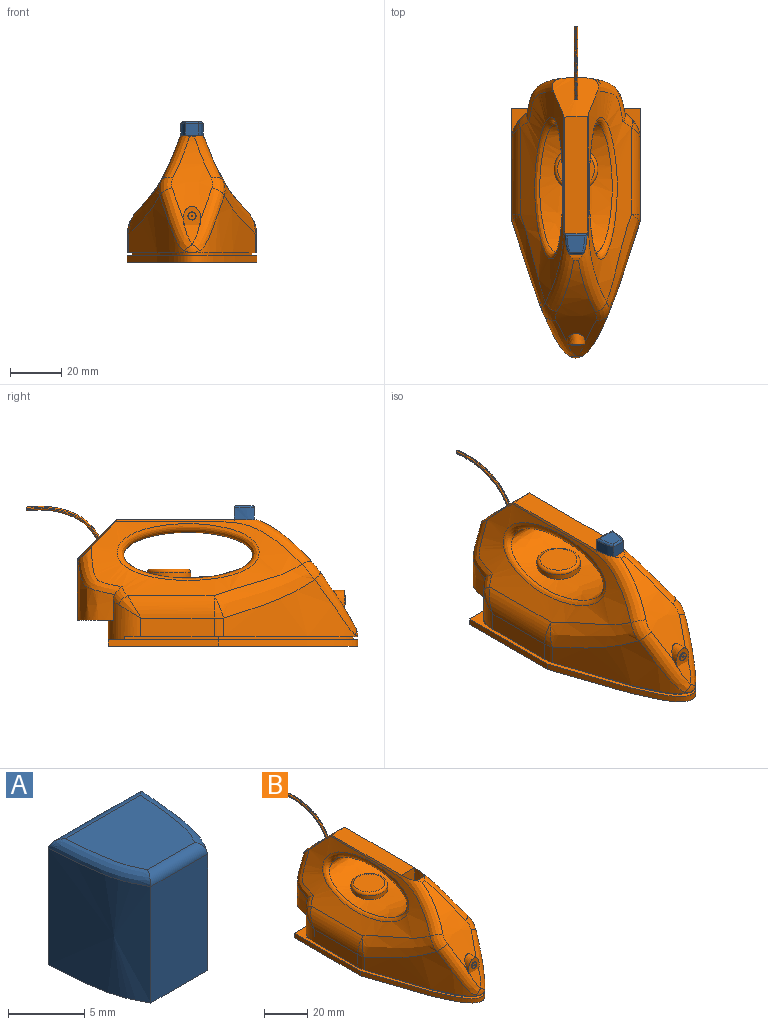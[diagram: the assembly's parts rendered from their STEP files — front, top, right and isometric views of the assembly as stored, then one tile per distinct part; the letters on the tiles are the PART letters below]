
ASSEMBLY  parts=2 mates=1
PART A: 10 faces, bbox 8.7x9.4x10.1 mm
  f0: extruded ~9.37x7.84mm, area 76.1mm2, adj f1,f3,f5,f6
  f1: plane 9.37x8.64mm, normal (0,1,0), area 81mm2, adj f0,f2,f5,f7
  f2: extruded ~9.37x7.84mm, area 76mm2, adj f1,f3,f5,f9
  f3: plane 9.37x5.27mm, normal (0,-1,0), area 49.4mm2, adj f0,f2,f5,f8
  f4: plane 7.01x6.32mm, normal (0,0,1), area 39mm2, adj f6,f7,f8,f9
  f5: plane 8.64x7.84mm, normal (0,0,-1), area 59.8mm2, adj f0,f1,f2,f3
  f6: bspline ~9.22x2.92mm, area 8.8mm2, adj f0,f4,f7,f8
  f7: cylinder r=0.76mm len=8.64mm, axis (1,0,0), area 9.4mm2, adj f1,f4,f6,f9
  f8: cylinder r=0.76mm len=5.27mm, axis (-1,0,0), area 5.8mm2, adj f3,f4,f6,f9
  f9: bspline ~8.95x2.65mm, area 8.8mm2, adj f2,f4,f7,f8
PART B: 393 faces, bbox 51x148.2x55 mm
  f0: extruded ~50.42x28.36mm, area 1593mm2, adj f1,f4,f385
  f1: cylinder r=8.53mm len=17.06mm, axis (0,0,-1), area 83.6mm2, adj f0,f2
  f2: torus R=7.26mm, axis (0,0,1), area 101.1mm2, adj f1,f3
  f3: plane 14.52x14.52mm, normal (0,0,1), area 165.5mm2, adj f2
  f4: bspline ~55.51x22.24mm, area 452.6mm2, adj f0,f5
  f5: extruded ~82.63x29.05mm, area 1122.6mm2, adj f4,f6,f371,f372,f373,f383,f384
  f6: cylinder r=12.7mm len=33.88mm, axis (0,-1,0), area 302mm2, adj f5,f7,f368,f369,f370
  f7: sphere r=12.7mm, area 19.5mm2, adj f6,f8,f384
  f8: cylinder r=12.7mm len=7.24mm, axis (0,0,-1), area 27.6mm2, adj f7,f9,f367,f370
  f9: extruded ~52.49x49.28mm, area 1568mm2, adj f8,f10,f363,f364,f365,f366,f367,f384
  f10: bspline ~26.09x17.79mm, area 161.3mm2, adj f9,f11,f361,f366
  f11: bspline ~9.71x9.08mm, area 43.1mm2, adj f10,f12,f361,f363
  f12: bspline ~128.84x21.82mm, area 228.3mm2, adj f11,f13,f18,f19,f360,f361,f373
  f13: extruded ~8.11x7.37mm, area 61.8mm2, adj f12,f14,f16,f17
  f14: plane 7.37x5.27mm, normal (0,1,0), area 38.8mm2, adj f13,f15,f16,f18
  f15: extruded ~8.11x7.37mm, area 61.8mm2, adj f14,f16,f17,f383
  f16: plane 8.83x8.28mm, normal (0,0,1), area 62.4mm2, adj f13,f14,f15,f17
  f17: plane 8.66x7.37mm, normal (0,-1,0), area 63.8mm2, adj f13,f15,f16,f360
  f18: cylinder r=5.08mm len=5.27mm, axis (1,0,0), area 7.6mm2, adj f12,f14,f361,f383
  f19: extruded ~82.58x29.05mm, area 1114.9mm2, adj f12,f20,f358,f359,f363,f373,f385
  f20: cylinder r=12.7mm len=33.88mm, axis (0,-1,0), area 302mm2, adj f19,f21,f22,f357
  f21: sphere r=12.7mm, area 17.5mm2, adj f20,f363,f364
  f22: plane 28.63x7.24mm, normal (-1,0,0), area 207.3mm2, adj f20,f23,f364,f367
  f23: cylinder r=12.7mm len=15.35mm, axis (0,0,-1), area 200.5mm2, adj f22,f24,f29,f354,f355,f356,f357,f358
  f24: plane 36.99x1.27mm, normal (-1,0,0), area 47mm2, adj f23,f25,f29,f367
  f25: extruded ~52.5x46.91mm, area 149.7mm2, adj f24,f26,f29,f367
  f26: plane 36.99x1.27mm, normal (1,0,0), area 47mm2, adj f25,f27,f29,f367
  f27: cylinder r=12.7mm len=15.35mm, axis (0,0,1), area 200.5mm2, adj f26,f28,f29,f354,f355,f367,f368,f369
  f28: extruded ~24.48x19.25mm, area 444.1mm2, adj f27,f355,f356,f371,f372,f373
  f29: plane 100.37x50.8mm, normal (0,0,1), area 392.8mm2, adj f23,f24,f25,f26,f27,f30,f352,f353
  f30: plane 43.25x2.54mm, normal (1,0,0), area 109.8mm2, adj f29,f31,f352,f354
  f31: plane 100.37x50.8mm, normal (0,0,-1), area 3110mm2, adj f30,f32,f34,f36,f38,f40,f42,f44
  f32: cylinder r=1.27mm len=2.54mm, axis (0,0,-1), area 12.2mm2, adj f31,f33
  f33: plane 2.54x2.54mm, normal (0,0,-1), area 5.1mm2, adj f32
  f34: cylinder r=1.27mm len=2.54mm, axis (0,0,-1), area 12.2mm2, adj f31,f35
  f35: plane 2.54x2.54mm, normal (0,0,-1), area 5.1mm2, adj f34
  f36: cylinder r=1.27mm len=2.54mm, axis (0,0,-1), area 12.2mm2, adj f31,f37
  f37: plane 2.54x2.54mm, normal (0,0,-1), area 5.1mm2, adj f36
  f38: cylinder r=1.27mm len=2.54mm, axis (0,0,-1), area 12.2mm2, adj f31,f39
  f39: plane 2.54x2.54mm, normal (0,0,-1), area 5.1mm2, adj f38
  f40: cylinder r=1.27mm len=2.54mm, axis (0,0,-1), area 12.2mm2, adj f31,f41
  f41: plane 2.54x2.54mm, normal (0,0,-1), area 5.1mm2, adj f40
  f42: cylinder r=1.27mm len=2.54mm, axis (0,0,-1), area 12.2mm2, adj f31,f43
  f43: plane 2.54x2.54mm, normal (0,0,-1), area 5.1mm2, adj f42
  f44: cylinder r=1.27mm len=2.54mm, axis (0,0,-1), area 12.2mm2, adj f31,f45
  f45: plane 2.54x2.54mm, normal (0,0,-1), area 5.1mm2, adj f44
  f46: cylinder r=1.27mm len=2.54mm, axis (0,0,-1), area 12.2mm2, adj f31,f47
  f47: plane 2.54x2.54mm, normal (0,0,-1), area 5.1mm2, adj f46
  f48: cylinder r=1.27mm len=2.54mm, axis (0,0,-1), area 12.2mm2, adj f31,f49
  f49: plane 2.54x2.54mm, normal (0,0,-1), area 5.1mm2, adj f48
  f50: cylinder r=1.27mm len=2.54mm, axis (0,0,-1), area 12.2mm2, adj f31,f51
  f51: plane 2.54x2.54mm, normal (0,0,-1), area 5.1mm2, adj f50
  f52: cylinder r=1.27mm len=2.54mm, axis (0,0,-1), area 12.2mm2, adj f31,f53
  f53: plane 2.54x2.54mm, normal (0,0,-1), area 5.1mm2, adj f52
  f54: cylinder r=1.27mm len=2.54mm, axis (0,0,-1), area 12.2mm2, adj f31,f55
  f55: plane 2.54x2.54mm, normal (0,0,-1), area 5.1mm2, adj f54
  f56: cylinder r=1.27mm len=2.54mm, axis (0,0,-1), area 12.2mm2, adj f31,f57
  f57: plane 2.54x2.54mm, normal (0,0,-1), area 5.1mm2, adj f56
  f58: cylinder r=1.27mm len=2.54mm, axis (0,0,-1), area 12.2mm2, adj f31,f59
  f59: plane 2.54x2.54mm, normal (0,0,-1), area 5.1mm2, adj f58
  f60: cylinder r=1.27mm len=2.54mm, axis (0,0,-1), area 12.2mm2, adj f31,f61
  f61: plane 2.54x2.54mm, normal (0,0,-1), area 5.1mm2, adj f60
  f62: cylinder r=1.27mm len=2.54mm, axis (0,0,-1), area 12.2mm2, adj f31,f63
  f63: plane 2.54x2.54mm, normal (0,0,-1), area 5.1mm2, adj f62
  f64: cylinder r=1.27mm len=2.54mm, axis (0,0,-1), area 12.2mm2, adj f31,f65
  f65: plane 2.54x2.54mm, normal (0,0,-1), area 5.1mm2, adj f64
  f66: cylinder r=1.27mm len=2.54mm, axis (0,0,-1), area 12.2mm2, adj f31,f67
  f67: plane 2.54x2.54mm, normal (0,0,-1), area 5.1mm2, adj f66
  f68: cylinder r=1.27mm len=2.54mm, axis (0,0,-1), area 12.2mm2, adj f31,f69
  f69: plane 2.54x2.54mm, normal (0,0,-1), area 5.1mm2, adj f68
  f70: cylinder r=1.27mm len=2.54mm, axis (0,0,-1), area 12.2mm2, adj f31,f71
  f71: plane 2.54x2.54mm, normal (0,0,-1), area 5.1mm2, adj f70
  f72: cylinder r=1.27mm len=2.54mm, axis (0,0,-1), area 12.2mm2, adj f31,f73
  f73: plane 2.54x2.54mm, normal (0,0,-1), area 5.1mm2, adj f72
  f74: cylinder r=1.27mm len=2.54mm, axis (0,0,-1), area 12.2mm2, adj f31,f75
  f75: plane 2.54x2.54mm, normal (0,0,-1), area 5.1mm2, adj f74
  f76: cylinder r=1.27mm len=2.54mm, axis (0,0,-1), area 12.2mm2, adj f31,f77
  f77: plane 2.54x2.54mm, normal (0,0,-1), area 5.1mm2, adj f76
  f78: cylinder r=1.27mm len=2.54mm, axis (0,0,-1), area 12.2mm2, adj f31,f79
  f79: plane 2.54x2.54mm, normal (0,0,-1), area 5.1mm2, adj f78
  f80: cylinder r=1.27mm len=2.54mm, axis (0,0,-1), area 12.2mm2, adj f31,f81
  f81: plane 2.54x2.54mm, normal (0,0,-1), area 5.1mm2, adj f80
  f82: cylinder r=1.27mm len=2.54mm, axis (0,0,-1), area 12.2mm2, adj f31,f83
  f83: plane 2.54x2.54mm, normal (0,0,-1), area 5.1mm2, adj f82
  f84: cylinder r=1.27mm len=2.54mm, axis (0,0,-1), area 12.2mm2, adj f31,f85
  f85: plane 2.54x2.54mm, normal (0,0,-1), area 5.1mm2, adj f84
  f86: cylinder r=1.27mm len=2.54mm, axis (0,0,-1), area 12.2mm2, adj f31,f87
  f87: plane 2.54x2.54mm, normal (0,0,-1), area 5.1mm2, adj f86
  f88: cylinder r=1.27mm len=2.54mm, axis (0,0,-1), area 12.2mm2, adj f31,f89
  f89: plane 2.54x2.54mm, normal (0,0,-1), area 5.1mm2, adj f88
  f90: cylinder r=1.27mm len=2.54mm, axis (0,0,-1), area 12.2mm2, adj f31,f91
  f91: plane 2.54x2.54mm, normal (0,0,-1), area 5.1mm2, adj f90
  f92: cylinder r=1.27mm len=2.54mm, axis (0,0,-1), area 12.2mm2, adj f31,f93
  f93: plane 2.54x2.54mm, normal (0,0,-1), area 5.1mm2, adj f92
  f94: cylinder r=1.27mm len=2.54mm, axis (0,0,-1), area 12.2mm2, adj f31,f95
  f95: plane 2.54x2.54mm, normal (0,0,-1), area 5.1mm2, adj f94
  f96: cylinder r=1.27mm len=2.54mm, axis (0,0,-1), area 12.2mm2, adj f31,f97
  f97: plane 2.54x2.54mm, normal (0,0,-1), area 5.1mm2, adj f96
  f98: cylinder r=1.27mm len=2.54mm, axis (0,0,-1), area 12.2mm2, adj f31,f99
  f99: plane 2.54x2.54mm, normal (0,0,-1), area 5.1mm2, adj f98
  f100: cylinder r=1.27mm len=2.54mm, axis (0,0,-1), area 12.2mm2, adj f31,f101
  f101: plane 2.54x2.54mm, normal (0,0,-1), area 5.1mm2, adj f100
  f102: cylinder r=1.27mm len=2.54mm, axis (0,0,-1), area 12.2mm2, adj f31,f103
  f103: plane 2.54x2.54mm, normal (0,0,-1), area 5.1mm2, adj f102
  f104: cylinder r=1.27mm len=2.54mm, axis (0,0,-1), area 12.2mm2, adj f31,f105
  f105: plane 2.54x2.54mm, normal (0,0,-1), area 5.1mm2, adj f104
  f106: cylinder r=1.27mm len=2.54mm, axis (0,0,-1), area 12.2mm2, adj f31,f107
  f107: plane 2.54x2.54mm, normal (0,0,-1), area 5.1mm2, adj f106
  f108: cylinder r=1.27mm len=2.54mm, axis (0,0,-1), area 12.2mm2, adj f31,f109
  f109: plane 2.54x2.54mm, normal (0,0,-1), area 5.1mm2, adj f108
  f110: cylinder r=1.27mm len=2.54mm, axis (0,0,-1), area 12.2mm2, adj f31,f111
  f111: plane 2.54x2.54mm, normal (0,0,-1), area 5.1mm2, adj f110
  f112: cylinder r=1.27mm len=2.54mm, axis (0,0,-1), area 12.2mm2, adj f31,f113
  f113: plane 2.54x2.54mm, normal (0,0,-1), area 5.1mm2, adj f112
  f114: cylinder r=1.27mm len=2.54mm, axis (0,0,-1), area 12.2mm2, adj f31,f115
  f115: plane 2.54x2.54mm, normal (0,0,-1), area 5.1mm2, adj f114
  f116: cylinder r=1.27mm len=2.54mm, axis (0,0,-1), area 12.2mm2, adj f31,f117
  f117: plane 2.54x2.54mm, normal (0,0,-1), area 5.1mm2, adj f116
  f118: cylinder r=1.27mm len=2.54mm, axis (0,0,-1), area 12.2mm2, adj f31,f119
  f119: plane 2.54x2.54mm, normal (0,0,-1), area 5.1mm2, adj f118
  f120: cylinder r=1.27mm len=2.54mm, axis (0,0,-1), area 12.2mm2, adj f31,f121
  f121: plane 2.54x2.54mm, normal (0,0,-1), area 5.1mm2, adj f120
  f122: cylinder r=1.27mm len=2.54mm, axis (0,0,-1), area 12.2mm2, adj f31,f123
  f123: plane 2.54x2.54mm, normal (0,0,-1), area 5.1mm2, adj f122
  f124: cylinder r=1.27mm len=2.54mm, axis (0,0,-1), area 12.2mm2, adj f31,f125
  f125: plane 2.54x2.54mm, normal (0,0,-1), area 5.1mm2, adj f124
  f126: cylinder r=1.27mm len=2.54mm, axis (0,0,-1), area 12.2mm2, adj f31,f127
  f127: plane 2.54x2.54mm, normal (0,0,-1), area 5.1mm2, adj f126
  f128: cylinder r=1.27mm len=2.54mm, axis (0,0,-1), area 12.2mm2, adj f31,f129
  f129: plane 2.54x2.54mm, normal (0,0,-1), area 5.1mm2, adj f128
  f130: cylinder r=1.27mm len=2.54mm, axis (0,0,-1), area 12.2mm2, adj f31,f131
  f131: plane 2.54x2.54mm, normal (0,0,-1), area 5.1mm2, adj f130
  f132: cylinder r=1.27mm len=2.54mm, axis (0,0,-1), area 12.2mm2, adj f31,f133
  f133: plane 2.54x2.54mm, normal (0,0,-1), area 5.1mm2, adj f132
  f134: cylinder r=1.27mm len=2.54mm, axis (0,0,-1), area 12.2mm2, adj f31,f135
  f135: plane 2.54x2.54mm, normal (0,0,-1), area 5.1mm2, adj f134
  f136: cylinder r=1.27mm len=2.54mm, axis (0,0,-1), area 12.2mm2, adj f31,f137
  f137: plane 2.54x2.54mm, normal (0,0,-1), area 5.1mm2, adj f136
  f138: cylinder r=1.27mm len=2.54mm, axis (0,0,-1), area 12.2mm2, adj f31,f139
  f139: plane 2.54x2.54mm, normal (0,0,-1), area 5.1mm2, adj f138
  f140: cylinder r=1.27mm len=2.54mm, axis (0,0,-1), area 12.2mm2, adj f31,f141
  f141: plane 2.54x2.54mm, normal (0,0,-1), area 5.1mm2, adj f140
  f142: cylinder r=1.27mm len=2.54mm, axis (0,0,-1), area 12.2mm2, adj f31,f143
  f143: plane 2.54x2.54mm, normal (0,0,-1), area 5.1mm2, adj f142
  f144: cylinder r=1.27mm len=2.54mm, axis (0,0,-1), area 12.2mm2, adj f31,f145
  f145: plane 2.54x2.54mm, normal (0,0,-1), area 5.1mm2, adj f144
  f146: cylinder r=1.27mm len=2.54mm, axis (0,0,-1), area 12.2mm2, adj f31,f147
  f147: plane 2.54x2.54mm, normal (0,0,-1), area 5.1mm2, adj f146
  f148: cylinder r=1.27mm len=2.54mm, axis (0,0,-1), area 12.2mm2, adj f31,f149
  f149: plane 2.54x2.54mm, normal (0,0,-1), area 5.1mm2, adj f148
  f150: cylinder r=1.27mm len=2.54mm, axis (0,0,-1), area 12.2mm2, adj f31,f151
  f151: plane 2.54x2.54mm, normal (0,0,-1), area 5.1mm2, adj f150
  f152: cylinder r=1.27mm len=2.54mm, axis (0,0,-1), area 12.2mm2, adj f31,f153
  f153: plane 2.54x2.54mm, normal (0,0,-1), area 5.1mm2, adj f152
  f154: cylinder r=1.27mm len=2.54mm, axis (0,0,-1), area 12.2mm2, adj f31,f155
  f155: plane 2.54x2.54mm, normal (0,0,-1), area 5.1mm2, adj f154
  f156: cylinder r=1.27mm len=2.54mm, axis (0,0,-1), area 12.2mm2, adj f31,f157
  f157: plane 2.54x2.54mm, normal (0,0,-1), area 5.1mm2, adj f156
  f158: cylinder r=1.27mm len=2.54mm, axis (0,0,-1), area 12.2mm2, adj f31,f159
  f159: plane 2.54x2.54mm, normal (0,0,-1), area 5.1mm2, adj f158
  f160: cylinder r=1.27mm len=2.54mm, axis (0,0,-1), area 12.2mm2, adj f31,f161
  f161: plane 2.54x2.54mm, normal (0,0,-1), area 5.1mm2, adj f160
  f162: cylinder r=1.27mm len=2.54mm, axis (0,0,-1), area 12.2mm2, adj f31,f163
  f163: plane 2.54x2.54mm, normal (0,0,-1), area 5.1mm2, adj f162
  f164: cylinder r=1.27mm len=2.54mm, axis (0,0,-1), area 12.2mm2, adj f31,f165
  f165: plane 2.54x2.54mm, normal (0,0,-1), area 5.1mm2, adj f164
  f166: cylinder r=1.27mm len=2.54mm, axis (0,0,-1), area 12.2mm2, adj f31,f167
  f167: plane 2.54x2.54mm, normal (0,0,-1), area 5.1mm2, adj f166
  f168: cylinder r=1.27mm len=2.54mm, axis (0,0,-1), area 12.2mm2, adj f31,f169
  f169: plane 2.54x2.54mm, normal (0,0,-1), area 5.1mm2, adj f168
  f170: cylinder r=1.27mm len=2.54mm, axis (0,0,-1), area 12.2mm2, adj f31,f171
  f171: plane 2.54x2.54mm, normal (0,0,-1), area 5.1mm2, adj f170
  f172: cylinder r=1.27mm len=2.54mm, axis (0,0,-1), area 12.2mm2, adj f31,f173
  f173: plane 2.54x2.54mm, normal (0,0,-1), area 5.1mm2, adj f172
  f174: cylinder r=1.27mm len=2.54mm, axis (0,0,-1), area 12.2mm2, adj f31,f175
  f175: plane 2.54x2.54mm, normal (0,0,-1), area 5.1mm2, adj f174
  f176: cylinder r=1.27mm len=2.54mm, axis (0,0,-1), area 12.2mm2, adj f31,f177
  f177: plane 2.54x2.54mm, normal (0,0,-1), area 5.1mm2, adj f176
  f178: cylinder r=1.27mm len=2.54mm, axis (0,0,-1), area 12.2mm2, adj f31,f179
  f179: plane 2.54x2.54mm, normal (0,0,-1), area 5.1mm2, adj f178
  f180: cylinder r=1.27mm len=2.54mm, axis (0,0,-1), area 12.2mm2, adj f31,f181
  f181: plane 2.54x2.54mm, normal (0,0,-1), area 5.1mm2, adj f180
  f182: cylinder r=1.27mm len=2.54mm, axis (0,0,-1), area 12.2mm2, adj f31,f183
  f183: plane 2.54x2.54mm, normal (0,0,-1), area 5.1mm2, adj f182
  f184: cylinder r=1.27mm len=2.54mm, axis (0,0,-1), area 12.2mm2, adj f31,f185
  f185: plane 2.54x2.54mm, normal (0,0,-1), area 5.1mm2, adj f184
  f186: cylinder r=1.27mm len=2.54mm, axis (0,0,-1), area 12.2mm2, adj f31,f187
  f187: plane 2.54x2.54mm, normal (0,0,-1), area 5.1mm2, adj f186
  f188: cylinder r=1.27mm len=2.54mm, axis (0,0,-1), area 12.2mm2, adj f31,f189
  f189: plane 2.54x2.54mm, normal (0,0,-1), area 5.1mm2, adj f188
  f190: cylinder r=1.27mm len=2.54mm, axis (0,0,-1), area 12.2mm2, adj f31,f191
  f191: plane 2.54x2.54mm, normal (0,0,-1), area 5.1mm2, adj f190
  f192: cylinder r=1.27mm len=2.54mm, axis (0,0,-1), area 12.2mm2, adj f31,f193
  f193: plane 2.54x2.54mm, normal (0,0,-1), area 5.1mm2, adj f192
  f194: cylinder r=1.27mm len=2.54mm, axis (0,0,-1), area 12.2mm2, adj f31,f195
  f195: plane 2.54x2.54mm, normal (0,0,-1), area 5.1mm2, adj f194
  f196: cylinder r=1.27mm len=2.54mm, axis (0,0,-1), area 12.2mm2, adj f31,f197
  f197: plane 2.54x2.54mm, normal (0,0,-1), area 5.1mm2, adj f196
  f198: cylinder r=1.27mm len=2.54mm, axis (0,0,-1), area 12.2mm2, adj f31,f199
  f199: plane 2.54x2.54mm, normal (0,0,-1), area 5.1mm2, adj f198
  f200: cylinder r=1.27mm len=2.54mm, axis (0,0,-1), area 12.2mm2, adj f31,f201
  f201: plane 2.54x2.54mm, normal (0,0,-1), area 5.1mm2, adj f200
  f202: cylinder r=1.27mm len=2.54mm, axis (0,0,-1), area 12.2mm2, adj f31,f203
  f203: plane 2.54x2.54mm, normal (0,0,-1), area 5.1mm2, adj f202
  f204: cylinder r=1.27mm len=2.54mm, axis (0,0,-1), area 12.2mm2, adj f31,f205
  f205: plane 2.54x2.54mm, normal (0,0,-1), area 5.1mm2, adj f204
  f206: cylinder r=1.27mm len=2.54mm, axis (0,0,-1), area 12.2mm2, adj f31,f207
  f207: plane 2.54x2.54mm, normal (0,0,-1), area 5.1mm2, adj f206
  f208: cylinder r=1.27mm len=2.54mm, axis (0,0,-1), area 12.2mm2, adj f31,f209
  f209: plane 2.54x2.54mm, normal (0,0,-1), area 5.1mm2, adj f208
  f210: cylinder r=1.27mm len=2.54mm, axis (0,0,-1), area 12.2mm2, adj f31,f211
  f211: plane 2.54x2.54mm, normal (0,0,-1), area 5.1mm2, adj f210
  f212: cylinder r=1.27mm len=2.54mm, axis (0,0,-1), area 12.2mm2, adj f31,f213
  f213: plane 2.54x2.54mm, normal (0,0,-1), area 5.1mm2, adj f212
  f214: cylinder r=1.27mm len=2.54mm, axis (0,0,-1), area 12.2mm2, adj f31,f215
  f215: plane 2.54x2.54mm, normal (0,0,-1), area 5.1mm2, adj f214
  f216: cylinder r=1.27mm len=2.54mm, axis (0,0,-1), area 12.2mm2, adj f31,f217
  f217: plane 2.54x2.54mm, normal (0,0,-1), area 5.1mm2, adj f216
  f218: cylinder r=1.27mm len=2.54mm, axis (0,0,-1), area 12.2mm2, adj f31,f219
  f219: plane 2.54x2.54mm, normal (0,0,-1), area 5.1mm2, adj f218
  f220: cylinder r=1.27mm len=2.54mm, axis (0,0,-1), area 12.2mm2, adj f31,f221
  f221: plane 2.54x2.54mm, normal (0,0,-1), area 5.1mm2, adj f220
  f222: cylinder r=1.27mm len=2.54mm, axis (0,0,-1), area 12.2mm2, adj f31,f223
  f223: plane 2.54x2.54mm, normal (0,0,-1), area 5.1mm2, adj f222
  f224: cylinder r=1.27mm len=2.54mm, axis (0,0,-1), area 12.2mm2, adj f31,f225
  f225: plane 2.54x2.54mm, normal (0,0,-1), area 5.1mm2, adj f224
  f226: cylinder r=1.27mm len=2.54mm, axis (0,0,-1), area 12.2mm2, adj f31,f227
  f227: plane 2.54x2.54mm, normal (0,0,-1), area 5.1mm2, adj f226
  f228: cylinder r=1.27mm len=2.54mm, axis (0,0,-1), area 12.2mm2, adj f31,f229
  f229: plane 2.54x2.54mm, normal (0,0,-1), area 5.1mm2, adj f228
  f230: cylinder r=1.27mm len=2.54mm, axis (0,0,-1), area 12.2mm2, adj f31,f231
  f231: plane 2.54x2.54mm, normal (0,0,-1), area 5.1mm2, adj f230
  f232: cylinder r=1.27mm len=2.54mm, axis (0,0,-1), area 12.2mm2, adj f31,f233
  f233: plane 2.54x2.54mm, normal (0,0,-1), area 5.1mm2, adj f232
  f234: cylinder r=1.27mm len=2.54mm, axis (0,0,-1), area 12.2mm2, adj f31,f235
  f235: plane 2.54x2.54mm, normal (0,0,-1), area 5.1mm2, adj f234
  f236: cylinder r=1.27mm len=2.54mm, axis (0,0,-1), area 12.2mm2, adj f31,f237
  f237: plane 2.54x2.54mm, normal (0,0,-1), area 5.1mm2, adj f236
  f238: cylinder r=1.27mm len=2.54mm, axis (0,0,-1), area 12.2mm2, adj f31,f239
  f239: plane 2.54x2.54mm, normal (0,0,-1), area 5.1mm2, adj f238
  f240: cylinder r=1.27mm len=2.54mm, axis (0,0,-1), area 12.2mm2, adj f31,f241
  f241: plane 2.54x2.54mm, normal (0,0,-1), area 5.1mm2, adj f240
  f242: cylinder r=1.27mm len=2.54mm, axis (0,0,-1), area 12.2mm2, adj f31,f243
  f243: plane 2.54x2.54mm, normal (0,0,-1), area 5.1mm2, adj f242
  f244: cylinder r=1.27mm len=2.54mm, axis (0,0,-1), area 12.2mm2, adj f31,f245
  f245: plane 2.54x2.54mm, normal (0,0,-1), area 5.1mm2, adj f244
  f246: cylinder r=1.27mm len=2.54mm, axis (0,0,-1), area 12.2mm2, adj f31,f247
  f247: plane 2.54x2.54mm, normal (0,0,-1), area 5.1mm2, adj f246
  f248: cylinder r=1.27mm len=2.54mm, axis (0,0,-1), area 12.2mm2, adj f31,f249
  f249: plane 2.54x2.54mm, normal (0,0,-1), area 5.1mm2, adj f248
  f250: cylinder r=1.27mm len=2.54mm, axis (0,0,-1), area 12.2mm2, adj f31,f251
  f251: plane 2.54x2.54mm, normal (0,0,-1), area 5.1mm2, adj f250
  f252: cylinder r=1.27mm len=2.54mm, axis (0,0,-1), area 12.2mm2, adj f31,f253
  f253: plane 2.54x2.54mm, normal (0,0,-1), area 5.1mm2, adj f252
  f254: cylinder r=1.27mm len=2.54mm, axis (0,0,-1), area 12.2mm2, adj f31,f255
  f255: plane 2.54x2.54mm, normal (0,0,-1), area 5.1mm2, adj f254
  f256: cylinder r=1.27mm len=2.54mm, axis (0,0,-1), area 12.2mm2, adj f31,f257
  f257: plane 2.54x2.54mm, normal (0,0,-1), area 5.1mm2, adj f256
  f258: cylinder r=1.27mm len=2.54mm, axis (0,0,-1), area 12.2mm2, adj f31,f259
  f259: plane 2.54x2.54mm, normal (0,0,-1), area 5.1mm2, adj f258
  f260: cylinder r=1.27mm len=2.54mm, axis (0,0,-1), area 12.2mm2, adj f31,f261
  f261: plane 2.54x2.54mm, normal (0,0,-1), area 5.1mm2, adj f260
  f262: cylinder r=1.27mm len=2.54mm, axis (0,0,-1), area 12.2mm2, adj f31,f263
  f263: plane 2.54x2.54mm, normal (0,0,-1), area 5.1mm2, adj f262
  f264: cylinder r=1.27mm len=2.54mm, axis (0,0,-1), area 12.2mm2, adj f31,f265
  f265: plane 2.54x2.54mm, normal (0,0,-1), area 5.1mm2, adj f264
  f266: cylinder r=1.27mm len=2.54mm, axis (0,0,-1), area 12.2mm2, adj f31,f267
  f267: plane 2.54x2.54mm, normal (0,0,-1), area 5.1mm2, adj f266
  f268: cylinder r=1.27mm len=2.54mm, axis (0,0,-1), area 12.2mm2, adj f31,f269
  f269: plane 2.54x2.54mm, normal (0,0,-1), area 5.1mm2, adj f268
  f270: cylinder r=1.27mm len=2.54mm, axis (0,0,-1), area 12.2mm2, adj f31,f271
  f271: plane 2.54x2.54mm, normal (0,0,-1), area 5.1mm2, adj f270
  f272: cylinder r=1.27mm len=2.54mm, axis (0,0,-1), area 12.2mm2, adj f31,f273
  f273: plane 2.54x2.54mm, normal (0,0,-1), area 5.1mm2, adj f272
  f274: cylinder r=1.27mm len=2.54mm, axis (0,0,-1), area 12.2mm2, adj f31,f275
  f275: plane 2.54x2.54mm, normal (0,0,-1), area 5.1mm2, adj f274
  f276: cylinder r=1.27mm len=2.54mm, axis (0,0,-1), area 12.2mm2, adj f31,f277
  f277: plane 2.54x2.54mm, normal (0,0,-1), area 5.1mm2, adj f276
  f278: cylinder r=1.27mm len=2.54mm, axis (0,0,-1), area 12.2mm2, adj f31,f279
  f279: plane 2.54x2.54mm, normal (0,0,-1), area 5.1mm2, adj f278
  f280: cylinder r=1.27mm len=2.54mm, axis (0,0,-1), area 12.2mm2, adj f31,f281
  f281: plane 2.54x2.54mm, normal (0,0,-1), area 5.1mm2, adj f280
  f282: cylinder r=1.27mm len=2.54mm, axis (0,0,-1), area 12.2mm2, adj f31,f283
  f283: plane 2.54x2.54mm, normal (0,0,-1), area 5.1mm2, adj f282
  f284: cylinder r=1.27mm len=2.54mm, axis (0,0,-1), area 12.2mm2, adj f31,f285
  f285: plane 2.54x2.54mm, normal (0,0,-1), area 5.1mm2, adj f284
  f286: cylinder r=1.27mm len=2.54mm, axis (0,0,-1), area 12.2mm2, adj f31,f287
  f287: plane 2.54x2.54mm, normal (0,0,-1), area 5.1mm2, adj f286
  f288: cylinder r=1.27mm len=2.54mm, axis (0,0,-1), area 12.2mm2, adj f31,f289
  f289: plane 2.54x2.54mm, normal (0,0,-1), area 5.1mm2, adj f288
  f290: cylinder r=1.27mm len=2.54mm, axis (0,0,-1), area 12.2mm2, adj f31,f291
  f291: plane 2.54x2.54mm, normal (0,0,-1), area 5.1mm2, adj f290
  f292: cylinder r=1.27mm len=2.54mm, axis (0,0,-1), area 12.2mm2, adj f31,f293
  f293: plane 2.54x2.54mm, normal (0,0,-1), area 5.1mm2, adj f292
  f294: cylinder r=1.27mm len=2.54mm, axis (0,0,-1), area 12.2mm2, adj f31,f295
  f295: plane 2.54x2.54mm, normal (0,0,-1), area 5.1mm2, adj f294
  f296: cylinder r=1.27mm len=2.54mm, axis (0,0,-1), area 12.2mm2, adj f31,f297
  f297: plane 2.54x2.54mm, normal (0,0,-1), area 5.1mm2, adj f296
  f298: cylinder r=1.27mm len=2.54mm, axis (0,0,-1), area 12.2mm2, adj f31,f299
  f299: plane 2.54x2.54mm, normal (0,0,-1), area 5.1mm2, adj f298
  f300: cylinder r=1.27mm len=2.54mm, axis (0,0,-1), area 12.2mm2, adj f31,f301
  f301: plane 2.54x2.54mm, normal (0,0,-1), area 5.1mm2, adj f300
  f302: cylinder r=1.27mm len=2.54mm, axis (0,0,-1), area 12.2mm2, adj f31,f303
  f303: plane 2.54x2.54mm, normal (0,0,-1), area 5.1mm2, adj f302
  f304: cylinder r=1.27mm len=2.54mm, axis (0,0,-1), area 12.2mm2, adj f31,f305
  f305: plane 2.54x2.54mm, normal (0,0,-1), area 5.1mm2, adj f304
  f306: cylinder r=1.27mm len=2.54mm, axis (0,0,-1), area 12.2mm2, adj f31,f307
  f307: plane 2.54x2.54mm, normal (0,0,-1), area 5.1mm2, adj f306
  f308: cylinder r=1.27mm len=2.54mm, axis (0,0,-1), area 12.2mm2, adj f31,f309
  f309: plane 2.54x2.54mm, normal (0,0,-1), area 5.1mm2, adj f308
  f310: cylinder r=1.27mm len=2.54mm, axis (0,0,-1), area 12.2mm2, adj f31,f311
  f311: plane 2.54x2.54mm, normal (0,0,-1), area 5.1mm2, adj f310
  f312: cylinder r=1.27mm len=2.54mm, axis (0,0,-1), area 12.2mm2, adj f31,f313
  f313: plane 2.54x2.54mm, normal (0,0,-1), area 5.1mm2, adj f312
  f314: cylinder r=1.27mm len=2.54mm, axis (0,0,-1), area 12.2mm2, adj f31,f315
  f315: plane 2.54x2.54mm, normal (0,0,-1), area 5.1mm2, adj f314
  f316: cylinder r=1.27mm len=2.54mm, axis (0,0,-1), area 12.2mm2, adj f31,f317
  f317: plane 2.54x2.54mm, normal (0,0,-1), area 5.1mm2, adj f316
  f318: cylinder r=1.27mm len=2.54mm, axis (0,0,-1), area 12.2mm2, adj f31,f319
  f319: plane 2.54x2.54mm, normal (0,0,-1), area 5.1mm2, adj f318
  f320: cylinder r=1.27mm len=2.54mm, axis (0,0,-1), area 12.2mm2, adj f31,f321
  f321: plane 2.54x2.54mm, normal (0,0,-1), area 5.1mm2, adj f320
  f322: cylinder r=1.27mm len=2.54mm, axis (0,0,-1), area 12.2mm2, adj f31,f323
  f323: plane 2.54x2.54mm, normal (0,0,-1), area 5.1mm2, adj f322
  f324: cylinder r=1.27mm len=2.54mm, axis (0,0,-1), area 12.2mm2, adj f31,f325
  f325: plane 2.54x2.54mm, normal (0,0,-1), area 5.1mm2, adj f324
  f326: cylinder r=1.27mm len=2.54mm, axis (0,0,-1), area 12.2mm2, adj f31,f327
  f327: plane 2.54x2.54mm, normal (0,0,-1), area 5.1mm2, adj f326
  f328: cylinder r=1.27mm len=2.54mm, axis (0,0,-1), area 12.2mm2, adj f31,f329
  f329: plane 2.54x2.54mm, normal (0,0,-1), area 5.1mm2, adj f328
  f330: cylinder r=1.27mm len=2.54mm, axis (0,0,-1), area 12.2mm2, adj f31,f331
  f331: plane 2.54x2.54mm, normal (0,0,-1), area 5.1mm2, adj f330
  f332: cylinder r=1.27mm len=2.54mm, axis (0,0,-1), area 12.2mm2, adj f31,f333
  f333: plane 2.54x2.54mm, normal (0,0,-1), area 5.1mm2, adj f332
  f334: cylinder r=1.27mm len=2.54mm, axis (0,0,-1), area 12.2mm2, adj f31,f335
  f335: plane 2.54x2.54mm, normal (0,0,-1), area 5.1mm2, adj f334
  f336: cylinder r=1.27mm len=2.54mm, axis (0,0,-1), area 12.2mm2, adj f31,f337
  f337: plane 2.54x2.54mm, normal (0,0,-1), area 5.1mm2, adj f336
  f338: cylinder r=1.27mm len=2.54mm, axis (0,0,-1), area 12.2mm2, adj f31,f339
  f339: plane 2.54x2.54mm, normal (0,0,-1), area 5.1mm2, adj f338
  f340: cylinder r=1.27mm len=2.54mm, axis (0,0,-1), area 12.2mm2, adj f31,f341
  f341: plane 2.54x2.54mm, normal (0,0,-1), area 5.1mm2, adj f340
  f342: cylinder r=1.27mm len=2.54mm, axis (0,0,-1), area 12.2mm2, adj f31,f343
  f343: plane 2.54x2.54mm, normal (0,0,-1), area 5.1mm2, adj f342
  f344: cylinder r=1.27mm len=2.54mm, axis (0,0,-1), area 12.2mm2, adj f31,f345
  f345: plane 2.54x2.54mm, normal (0,0,-1), area 5.1mm2, adj f344
  f346: cylinder r=1.27mm len=2.54mm, axis (0,0,-1), area 12.2mm2, adj f31,f347
  f347: plane 2.54x2.54mm, normal (0,0,-1), area 5.1mm2, adj f346
  f348: cylinder r=1.27mm len=2.54mm, axis (0,0,-1), area 12.2mm2, adj f31,f349
  f349: plane 2.54x2.54mm, normal (0,0,-1), area 5.1mm2, adj f348
  f350: cylinder r=1.27mm len=2.54mm, axis (0,0,-1), area 12.2mm2, adj f31,f351
  f351: plane 2.54x2.54mm, normal (0,0,-1), area 5.1mm2, adj f350
  f352: extruded ~54.29x50.8mm, area 312.3mm2, adj f29,f30,f31,f353
  f353: plane 43.25x2.54mm, normal (-1,0,0), area 109.8mm2, adj f29,f31,f352,f354
  f354: plane 50.8x10.16mm, normal (0,1,0), area 319.7mm2, adj f23,f27,f29,f30,f31,f353,f355
  f355: plane 38.99x14.31mm, normal (0,0,-1), area 380.6mm2, adj f23,f27,f28,f354,f356
  f356: extruded ~24.13x19.25mm, area 443.1mm2, adj f23,f28,f355,f358,f359,f373
  f357: bspline ~9.27x9.27mm, area 18.9mm2, adj f20,f23,f358
  f358: bspline ~9.09x8.55mm, area 27.2mm2, adj f19,f23,f356,f357,f359
  f359: bspline ~23.47x21.24mm, area 145.2mm2, adj f19,f356,f358,f373
  f360: plane 48.41x8.9mm, normal (0,0,1), area 406.7mm2, adj f12,f17,f373,f383
  f361: extruded ~42.12x37.47mm, area 477.4mm2, adj f10,f11,f12,f18,f362,f365,f383
  f362: bspline ~9.92x9.02mm, area 43.1mm2, adj f361,f365,f383,f384
  f363: bspline ~41.71x22.29mm, area 370.5mm2, adj f9,f11,f19,f21
  f364: cylinder r=12.7mm len=7.24mm, axis (0,0,-1), area 27.6mm2, adj f9,f21,f22,f367
  f365: bspline ~29.24x20.38mm, area 161.3mm2, adj f9,f361,f362,f366
  f366: bspline ~5.75x3.04mm, area 7.1mm2, adj f9,f10,f365
  f367: plane 94.03x50.42mm, normal (0,0,-1), area 294.7mm2, adj f8,f9,f22,f23,f24,f25,f26,f27
  f368: bspline ~5.24x5.24mm, area 2.5mm2, adj f6,f27
  f369: bspline ~7.3x7.3mm, area 11.8mm2, adj f6,f27,f371
  f370: plane 28.63x7.24mm, normal (1,0,0), area 207.3mm2, adj f6,f8,f27,f367
  f371: bspline ~9.09x8.55mm, area 27.2mm2, adj f5,f27,f28,f369,f372
  f372: bspline ~23.43x20.45mm, area 150.9mm2, adj f5,f28,f371,f373
  f373: bspline ~21.01x15.93mm, area 304.3mm2, adj f5,f12,f19,f28,f356,f359,f360,f372
  f374: bspline ~28.92x12.25mm, area 25.4mm2, adj f373,f375,f376,f382
  f375: plane 1.49x1.29mm, normal (0,1,-0.01), area 1.6mm2, adj f374,f376,f377,f378,f379,f380,f381,f382
  f376: extruded ~27.7x11.41mm, area 8.1mm2, adj f373,f374,f375,f377
  f377: bspline ~28.92x12.25mm, area 25.4mm2, adj f373,f375,f376,f378
  f378: plane 28.41x12.01mm, normal (-1,0,0), area 14mm2, adj f373,f375,f377,f379
  f379: bspline ~33.88x17.12mm, area 26.1mm2, adj f373,f375,f378,f380
  f380: extruded ~28.77x11.82mm, area 8.3mm2, adj f373,f375,f379,f381
  f381: bspline ~33.88x17.11mm, area 26.1mm2, adj f373,f375,f380,f382
  f382: plane 28.41x12.01mm, normal (1,0,0), area 14mm2, adj f373,f374,f375,f381
  f383: bspline ~128.84x21.82mm, area 228.5mm2, adj f5,f15,f18,f360,f361,f362,f373
  f384: bspline ~41.71x22.29mm, area 370.5mm2, adj f5,f7,f9,f362
  f385: bspline ~55.51x22.24mm, area 452.5mm2, adj f0,f19
  f386: extruded ~7.09x7.03mm, area 49mm2, adj f387,f392
  f387: plane 7.09x7.03mm, normal (0,-1,0), area 33.9mm2, adj f386,f388,f392
  f388: cylinder r=1.58mm len=3.16mm, axis (0,1,0), area 4.5mm2, adj f387,f389
  f389: plane 3.16x3.16mm, normal (0,-1,0), area 7.4mm2, adj f388,f390
  f390: cylinder r=0.38mm len=12.25mm, axis (0,-1,0), area 28.9mm2, adj f389,f391
  f391: cone r=0mm half-angle=59deg, axis (0,-1,0), area 0.5mm2, adj f390
  f392: extruded ~7.09x7.03mm, area 44.5mm2, adj f386,f387
PLACE A t=(-2.24,18.34,19.12)mm
PLACE B t=(-2.24,18.07,16.44)mm
MATE fastened A.f1 <-> B.f17  axis (0,1,0) through (-2.24,12.15,65.97)mm
